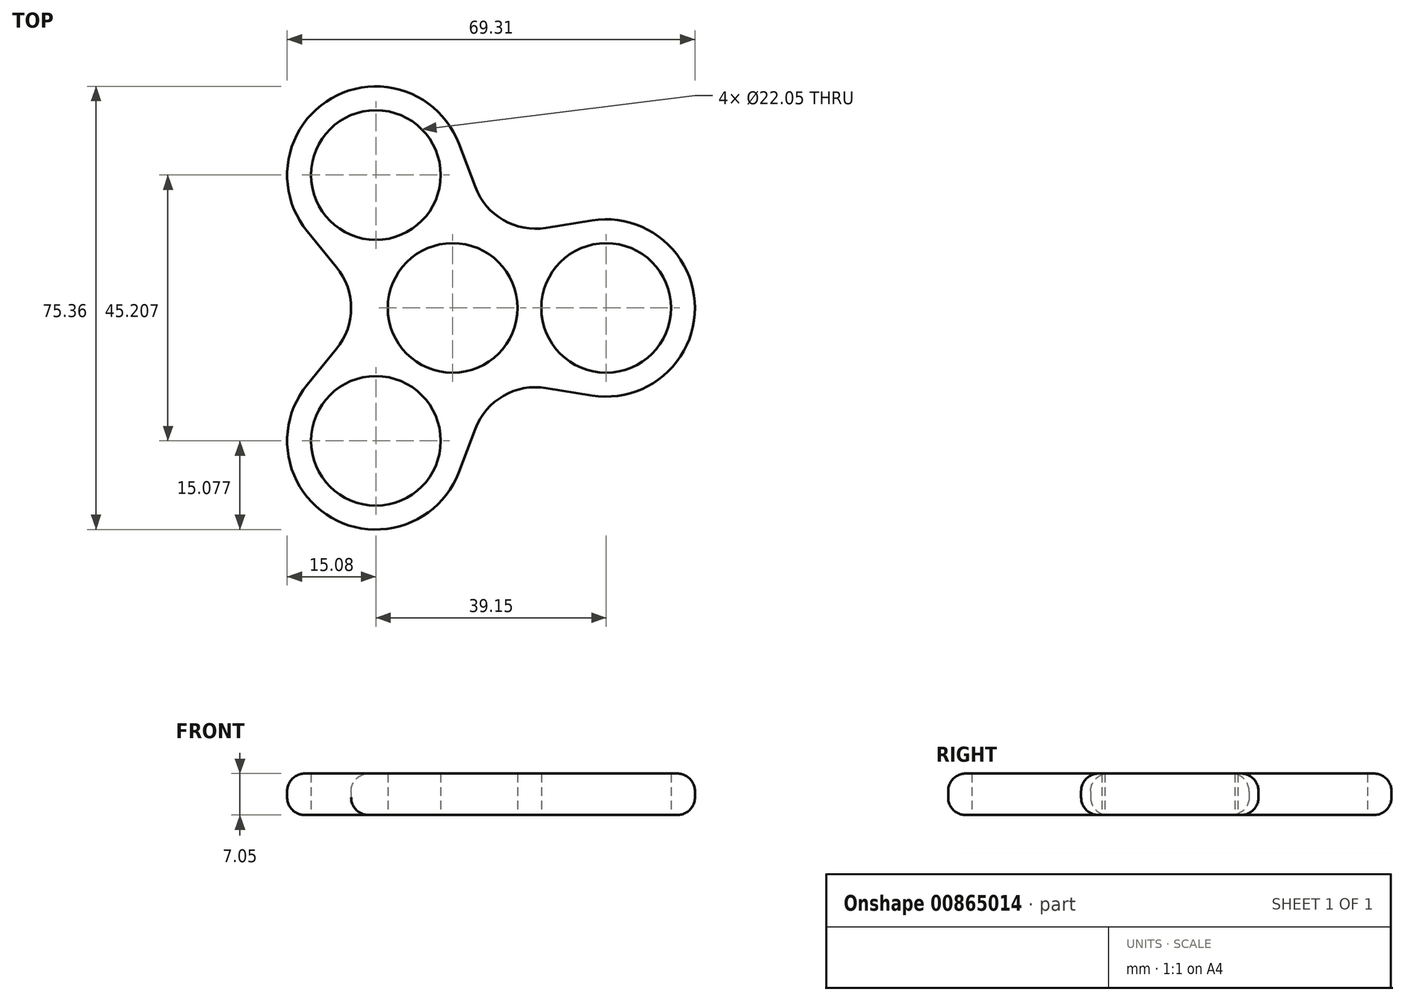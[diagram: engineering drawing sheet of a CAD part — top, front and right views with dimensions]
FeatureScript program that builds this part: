
annotation { "Feature Type Name" : "Feature", "Feature Type Description" : "" }
export const myFeature = defineFeature(function(context is Context, id is Id, definition is map)
    precondition{}
    {
        {
            var Q0;
            Q0=qCreatedBy(makeId("Top.planeOp"),FACE);
            var sketch = newSketch(context, id + "F0", { "sketchPlane" : qUnion([Q0])});
            skCircle(sketch, "E0", {"center": v(0, 0) * mm, "radius": 11.03 * mm});
            skLineSegment(sketch, "E1", {"start": v(0, 0) * mm, "end": v(26.1, 0) * mm, "construction": true});
            skCircle(sketch, "E2", {"center": v(26.1, 0) * mm, "radius": 11.03 * mm});
            skLineSegment(sketch, "E3", {"start": v(15.9, -13.61) * mm, "end": v(23.67, -14.88) * mm});
            skLineSegment(sketch, "E4", {"start": v(15.9, 13.61) * mm, "end": v(23.67, 14.88) * mm});
            skArc(sketch, "E5", {"start": v(23.67, -14.88) * mm, "mid": v(41.18, 0) * mm, "end": v(23.67, 14.88) * mm});
            skLineSegment(sketch, "E6.1.0", {"start": v(0, 0) * mm, "end": v(-13.05, 22.6) * mm, "construction": true});
            skArc(sketch, "E6.1.1", {"start": v(1.05, 27.94) * mm, "mid": v(-20.59, 35.66) * mm, "end": v(-24.72, 13.06) * mm});
            skLineSegment(sketch, "E6.1.2", {"start": v(3.84, 20.57) * mm, "end": v(1.05, 27.94) * mm});
            skCircle(sketch, "E6.1.3", {"center": v(-13.05, 22.6) * mm, "radius": 11.03 * mm});
            skLineSegment(sketch, "E6.1.4", {"start": v(-19.74, 6.96) * mm, "end": v(-24.72, 13.06) * mm});
            skLineSegment(sketch, "E6.2.0", {"start": v(0, 0) * mm, "end": v(-13.05, -22.6) * mm, "construction": true});
            skArc(sketch, "E6.2.1", {"start": v(-24.72, -13.06) * mm, "mid": v(-20.59, -35.66) * mm, "end": v(1.05, -27.94) * mm});
            skLineSegment(sketch, "E6.2.2", {"start": v(-19.74, -6.96) * mm, "end": v(-24.72, -13.06) * mm});
            skCircle(sketch, "E6.2.3", {"center": v(-13.05, -22.6) * mm, "radius": 11.03 * mm});
            skLineSegment(sketch, "E6.2.4", {"start": v(3.84, -20.57) * mm, "end": v(1.05, -27.94) * mm});
            skPoint(sketch, "E7.orphan", {"position": v(0, 11.03) * mm});
            skPoint(sketch, "E8.orphan", {"position": v(9.55, 5.51) * mm});
            skPoint(sketch, "E9.orphan", {"position": v(-9.55, 5.51) * mm});
            skPoint(sketch, "E10.orphan", {"position": v(-9.55, -5.51) * mm});
            skPoint(sketch, "E11.orphan", {"position": v(0, -11.03) * mm});
            skPoint(sketch, "E12.orphan", {"position": v(9.55, -5.51) * mm});
            skPoint(sketch, "E13.visualSharp", {"position": v(7.03, 12.17) * mm});
            skArc(sketch, "E13.filletArc", {"start": v(3.84, 20.57) * mm, "mid": v(8.63, 14.94) * mm, "end": v(15.9, 13.61) * mm});
            skPoint(sketch, "E14.visualSharp", {"position": v(7.03, -12.17) * mm});
            skArc(sketch, "E14.filletArc", {"start": v(15.9, -13.61) * mm, "mid": v(8.63, -14.94) * mm, "end": v(3.84, -20.57) * mm});
            skPoint(sketch, "E15.visualSharp", {"position": v(-14.05, 0) * mm});
            skArc(sketch, "E15.filletArc", {"start": v(-19.74, -6.96) * mm, "mid": v(-17.26, 0) * mm, "end": v(-19.74, 6.96) * mm});
            skSolve(sketch);
        }
        {
            var Q0;
            Q0 = qSketchRegion(id + "F0", true);
            extrude(context, id + "F1", {"entities" : qUnion([Q0]), "depth" : 7.05 * mm, "offsetDistance" : 25 * mm});
        }
        {
            var Q0;
            Q0=makeQuery(id+"F1.opExtrude","CAP_EDGE",EDGE,{"disambiguationData":[OSD([sQuery(id+"F0.wireOp",EDGE,"E14.filletArc")])],"isStart":false});
            var Q1;
            Q1=makeQuery(id+"F1.opExtrude","CAP_EDGE",EDGE,{"disambiguationData":[OSD([sQuery(id+"F0.wireOp",EDGE,"E14.filletArc")])],"isStart":true});
            var Q2;
            Q2=makeQuery(id+"F1.opExtrude","CAP_EDGE",EDGE,{"disambiguationData":[OSD([sQuery(id+"F0.wireOp",EDGE,"E13.filletArc")])],"isStart":true});
            var Q3;
            Q3=makeQuery(id+"F1.opExtrude","CAP_EDGE",EDGE,{"disambiguationData":[OSD([sQuery(id+"F0.wireOp",EDGE,"E15.filletArc")])],"isStart":true});
            var Q4;
            Q4=makeQuery(id+"F1.opExtrude","CAP_EDGE",EDGE,{"disambiguationData":[OSD([sQuery(id+"F0.wireOp",EDGE,"E13.filletArc")])],"isStart":false});
            var Q5;
            Q5=makeQuery(id+"F1.opExtrude","CAP_EDGE",EDGE,{"disambiguationData":[OSD([sQuery(id+"F0.wireOp",EDGE,"E15.filletArc")])],"isStart":false});
            fillet(context, id + "F2", {"entities" : qUnion([Q0, Q1, Q2, Q3, Q4, Q5]), "radius" : 3 * mm, "tangentPropagation" : true, "allowEdgeOverflow" : false});
        }
    });
